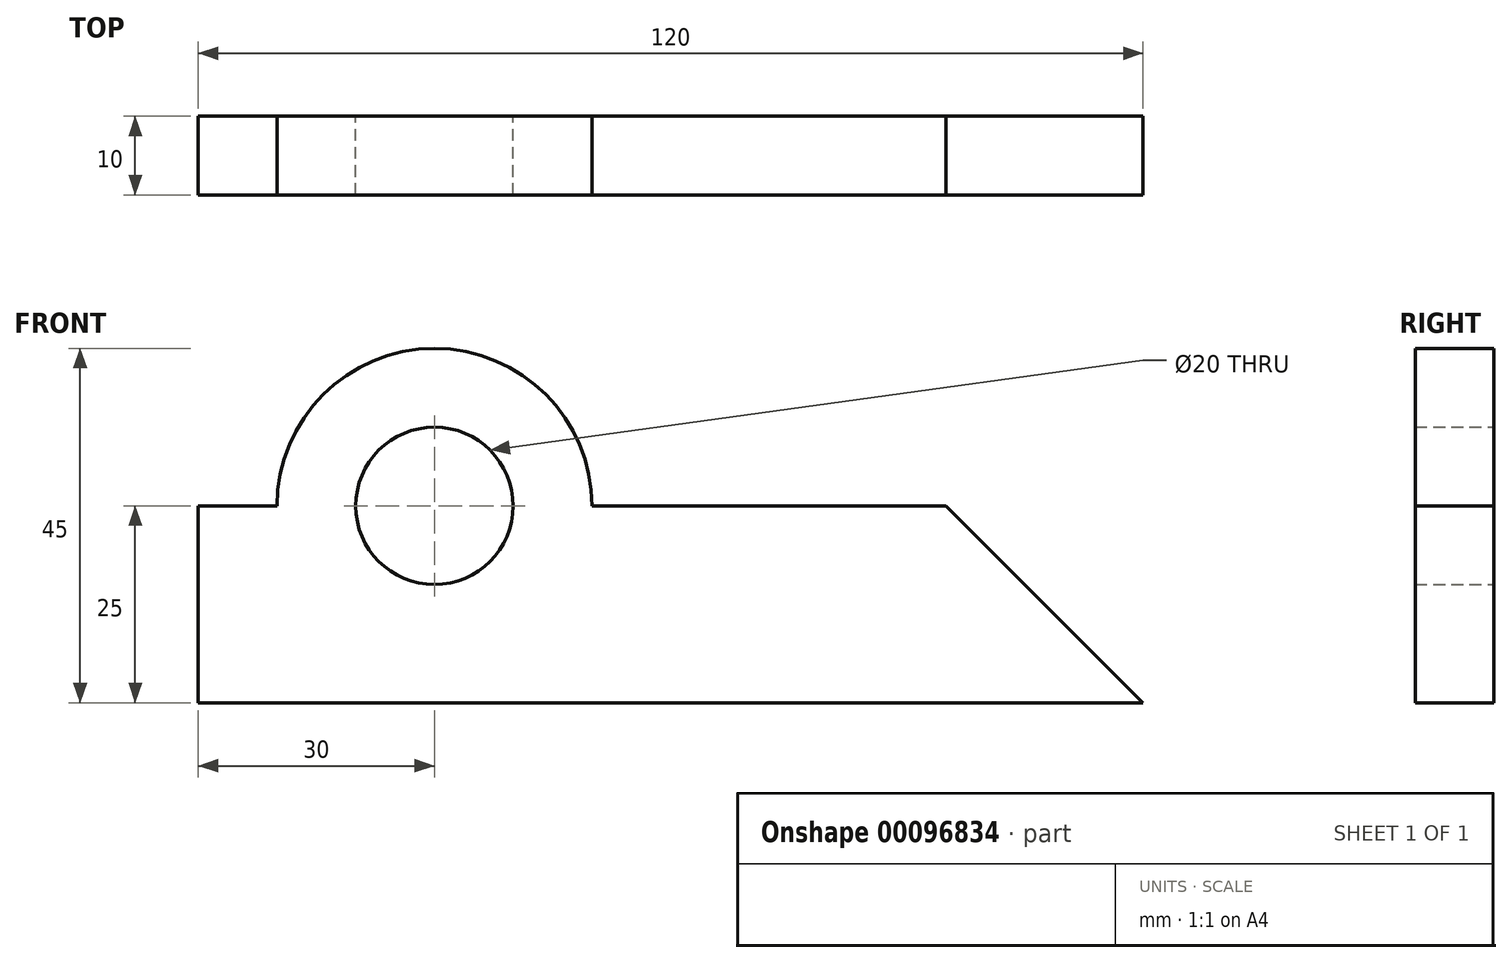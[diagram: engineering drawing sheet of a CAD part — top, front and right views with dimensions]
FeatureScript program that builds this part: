
annotation { "Feature Type Name" : "Feature", "Feature Type Description" : "" }
export const myFeature = defineFeature(function(context is Context, id is Id, definition is map)
    precondition{}
    {
        {
            var Q0;
            Q0=qCreatedBy(makeId("Front.planeOp"),FACE);
            var sketch = newSketch(context, id + "F0", { "sketchPlane" : qUnion([Q0])});
            skLineSegment(sketch, "E0", {"start": v(0, 0) * mm, "end": v(0, 25) * mm});
            skLineSegment(sketch, "E1", {"start": v(0, 0) * mm, "end": v(120, 0) * mm});
            skArc(sketch, "E2", {"start": v(50, 25) * mm, "mid": v(30, 45) * mm, "end": v(10, 25) * mm});
            skCircle(sketch, "E3", {"center": v(30, 25) * mm, "radius": 10 * mm});
            skLineSegment(sketch, "E4", {"start": v(0, 25) * mm, "end": v(10, 25) * mm});
            skLineSegment(sketch, "E5", {"start": v(50, 25) * mm, "end": v(95, 25) * mm});
            skLineSegment(sketch, "E6", {"start": v(120, 0) * mm, "end": v(95, 25) * mm});
            skSolve(sketch);
        }
        {
            var Q0;
            Q0 = qSketchRegion(id + "F0", true);
            extrude(context, id + "F1", {"entities" : qUnion([Q0]), "depth" : 10 * mm});
        }
    });
